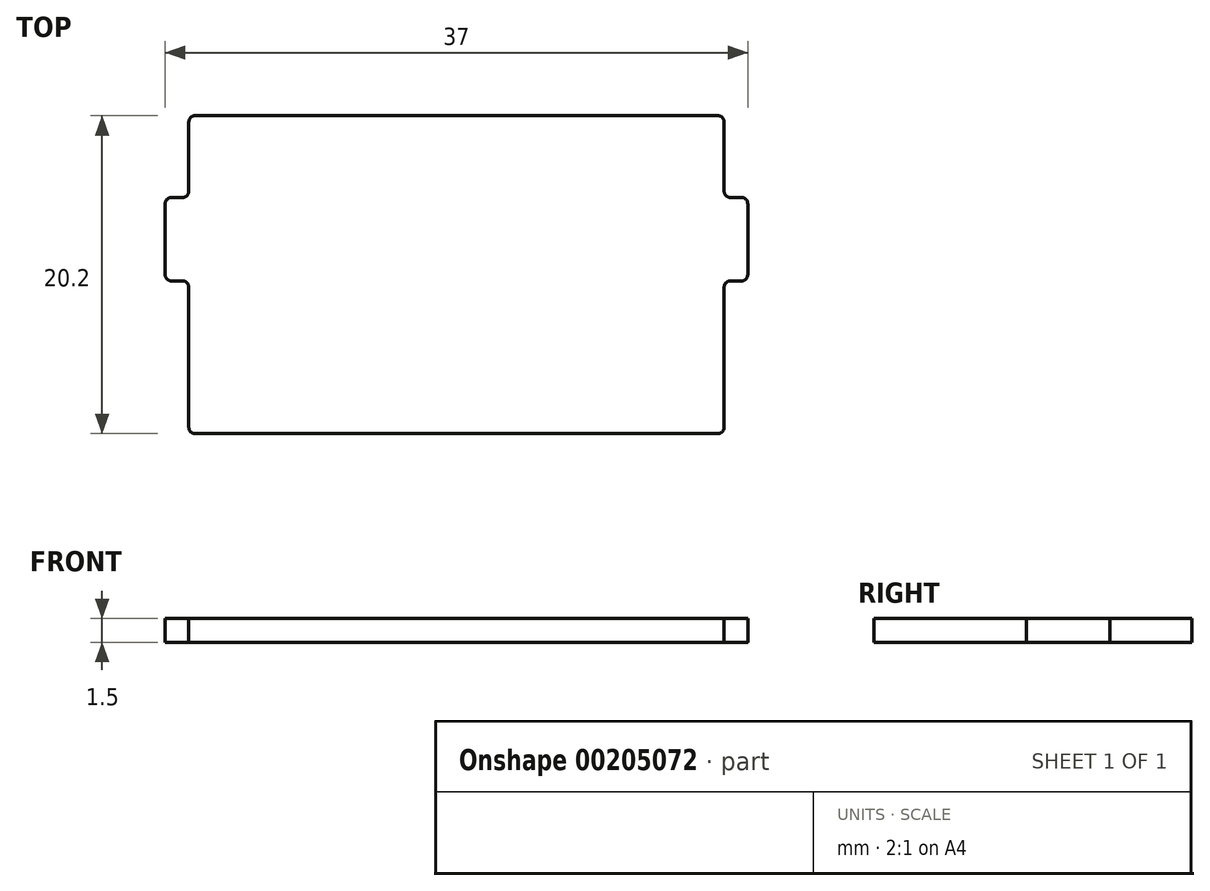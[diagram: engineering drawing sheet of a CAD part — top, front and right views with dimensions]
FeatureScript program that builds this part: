
annotation { "Feature Type Name" : "Feature", "Feature Type Description" : "" }
export const myFeature = defineFeature(function(context is Context, id is Id, definition is map)
    precondition{}
    {
        {
            var Q0;
            Q0=qCreatedBy(makeId("Top.planeOp"),FACE);
            var sketch = newSketch(context, id + "F0", { "sketchPlane" : qUnion([Q0])});
            skLineSegment(sketch, "E0", {"start": v(0, -0.4) * mm, "end": v(0, -9.3) * mm});
            skLineSegment(sketch, "E1", {"start": v(-0.4, -9.7) * mm, "end": v(-33.6, -9.7) * mm});
            skLineSegment(sketch, "E2", {"start": v(-34, -9.3) * mm, "end": v(-34, -0.4) * mm});
            skLineSegment(sketch, "E3", {"start": v(-34.4, 0) * mm, "end": v(-35.1, 0) * mm});
            skLineSegment(sketch, "E4", {"start": v(-35.5, 0.4) * mm, "end": v(-35.5, 4.9) * mm});
            skLineSegment(sketch, "E5", {"start": v(-35.1, 5.3) * mm, "end": v(-34.4, 5.3) * mm});
            skLineSegment(sketch, "E6", {"start": v(-34, 5.7) * mm, "end": v(-34, 10.1) * mm});
            skLineSegment(sketch, "E7", {"start": v(-33.6, 10.5) * mm, "end": v(-0.4, 10.5) * mm});
            skLineSegment(sketch, "E8", {"start": v(0, 10.1) * mm, "end": v(0, 5.7) * mm});
            skLineSegment(sketch, "E9", {"start": v(0.4, 5.3) * mm, "end": v(1.1, 5.3) * mm});
            skLineSegment(sketch, "E10", {"start": v(1.5, 4.9) * mm, "end": v(1.5, 0.4) * mm});
            skLineSegment(sketch, "E11", {"start": v(1.1, 0) * mm, "end": v(0.4, 0) * mm});
            skPoint(sketch, "E12.visualSharp", {"position": v(0, 10.5) * mm});
            skArc(sketch, "E12.filletArc", {"start": v(0, 10.1) * mm, "mid": v(-0.12, 10.38) * mm, "end": v(-0.4, 10.5) * mm});
            skPoint(sketch, "E13.visualSharp", {"position": v(0, 5.3) * mm});
            skArc(sketch, "E13.filletArc", {"start": v(0, 5.7) * mm, "mid": v(0.12, 5.42) * mm, "end": v(0.4, 5.3) * mm});
            skPoint(sketch, "E14.visualSharp", {"position": v(1.5, 0) * mm});
            skArc(sketch, "E14.filletArc", {"start": v(1.1, 0) * mm, "mid": v(1.38, 0.12) * mm, "end": v(1.5, 0.4) * mm});
            skPoint(sketch, "E15.visualSharp", {"position": v(1.5, 5.3) * mm});
            skArc(sketch, "E15.filletArc", {"start": v(1.5, 4.9) * mm, "mid": v(1.38, 5.18) * mm, "end": v(1.1, 5.3) * mm});
            skPoint(sketch, "E16.visualSharp", {"position": v(0, 0) * mm});
            skArc(sketch, "E16.filletArc", {"start": v(0.4, 0) * mm, "mid": v(0.12, -0.12) * mm, "end": v(0, -0.4) * mm});
            skPoint(sketch, "E17.visualSharp", {"position": v(0, -9.7) * mm});
            skArc(sketch, "E17.filletArc", {"start": v(-0.4, -9.7) * mm, "mid": v(-0.12, -9.58) * mm, "end": v(0, -9.3) * mm});
            skPoint(sketch, "E18.visualSharp", {"position": v(-34, -9.7) * mm});
            skArc(sketch, "E18.filletArc", {"start": v(-34, -9.3) * mm, "mid": v(-33.88, -9.58) * mm, "end": v(-33.6, -9.7) * mm});
            skPoint(sketch, "E19.visualSharp", {"position": v(-34, 0) * mm});
            skArc(sketch, "E19.filletArc", {"start": v(-34, -0.4) * mm, "mid": v(-34.12, -0.12) * mm, "end": v(-34.4, 0) * mm});
            skPoint(sketch, "E20.visualSharp", {"position": v(-35.5, 5.3) * mm});
            skArc(sketch, "E20.filletArc", {"start": v(-35.1, 5.3) * mm, "mid": v(-35.38, 5.18) * mm, "end": v(-35.5, 4.9) * mm});
            skPoint(sketch, "E21.visualSharp", {"position": v(-35.5, 0) * mm});
            skArc(sketch, "E21.filletArc", {"start": v(-35.5, 0.4) * mm, "mid": v(-35.38, 0.12) * mm, "end": v(-35.1, 0) * mm});
            skPoint(sketch, "E22.visualSharp", {"position": v(-34, 5.3) * mm});
            skArc(sketch, "E22.filletArc", {"start": v(-34.4, 5.3) * mm, "mid": v(-34.12, 5.42) * mm, "end": v(-34, 5.7) * mm});
            skPoint(sketch, "E23.visualSharp", {"position": v(-34, 10.5) * mm});
            skArc(sketch, "E23.filletArc", {"start": v(-33.6, 10.5) * mm, "mid": v(-33.88, 10.38) * mm, "end": v(-34, 10.1) * mm});
            skSolve(sketch);
        }
        {
            var Q0;
            Q0 = qSketchRegion(id + "F0", true);
            extrude(context, id + "F1", {"entities" : qUnion([Q0]), "depth" : 1.5 * mm});
        }
    });
